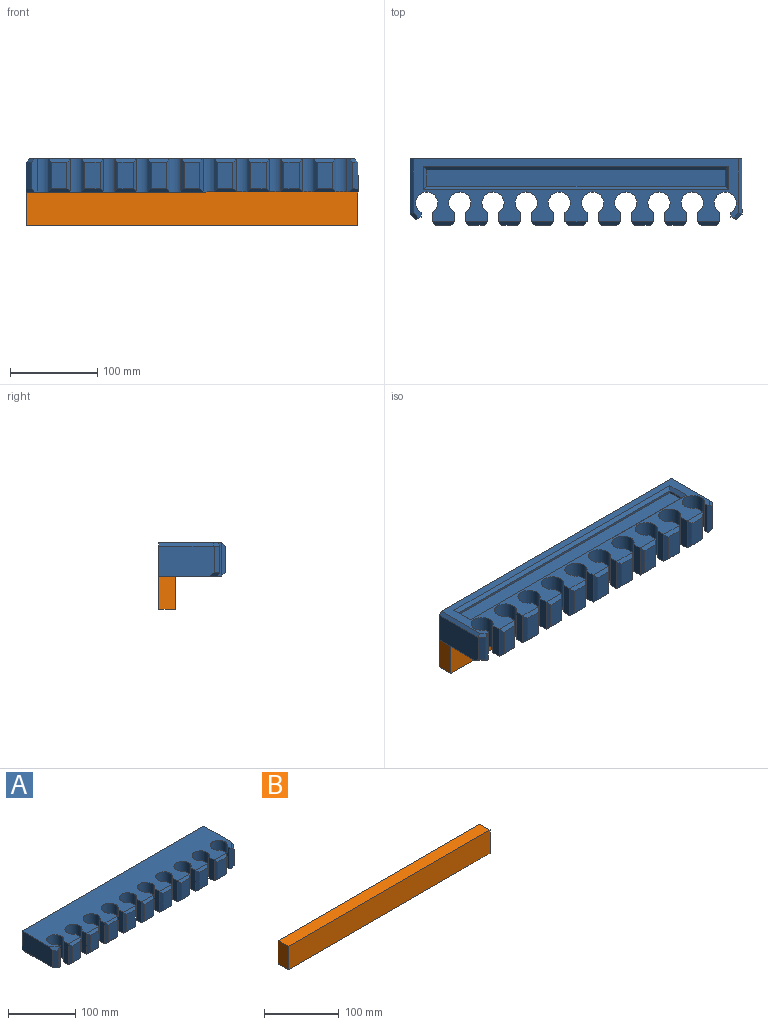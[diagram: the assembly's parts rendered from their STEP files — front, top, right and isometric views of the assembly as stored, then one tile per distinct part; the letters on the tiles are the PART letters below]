
ASSEMBLY  parts=2 mates=1
PART A: 99 faces, bbox 381x76.2x38.1 mm
  f0: plane 38.1x10.59mm, normal (-1,0,0), area 403.5mm2, adj f47,f48,f49,f86
  f1: plane 30.48x17.78mm, normal (0,-1,0), area 541.9mm2, adj f83,f84,f85,f86
  f2: plane 38.1x10.59mm, normal (1,0,0), area 403.5mm2, adj f3,f48,f49,f83
  f3: cylinder r=12.7mm len=38.1mm, axis (0,0,1), area 2533.5mm2, adj f2,f4,f48,f49
  f4: plane 38.1x10.59mm, normal (-1,0,0), area 403.5mm2, adj f3,f48,f49,f82
  f5: plane 30.48x17.78mm, normal (0,-1,0), area 541.9mm2, adj f79,f80,f81,f82
  f6: plane 38.1x10.59mm, normal (1,0,0), area 403.5mm2, adj f7,f48,f49,f79
  f7: cylinder r=12.7mm len=38.1mm, axis (0,0,1), area 2533.5mm2, adj f6,f8,f48,f49
  f8: plane 38.1x10.59mm, normal (-1,0,0), area 403.5mm2, adj f7,f48,f49,f78
  f9: plane 30.48x17.78mm, normal (0,-1,0), area 541.9mm2, adj f75,f76,f77,f78
  f10: plane 38.1x10.59mm, normal (1,0,0), area 403.5mm2, adj f11,f48,f49,f75
  f11: cylinder r=12.7mm len=38.1mm, axis (0,0,1), area 2533.5mm2, adj f10,f12,f48,f49
  f12: plane 38.1x10.59mm, normal (-1,0,0), area 403.5mm2, adj f11,f48,f49,f74
  f13: plane 30.48x17.78mm, normal (0,-1,0), area 541.9mm2, adj f71,f72,f73,f74
  f14: plane 38.1x10.59mm, normal (1,0,0), area 403.5mm2, adj f15,f48,f49,f71
  f15: cylinder r=12.7mm len=38.1mm, axis (0,0,1), area 2533.5mm2, adj f14,f16,f48,f49
  f16: plane 38.1x10.59mm, normal (-1,0,0), area 403.5mm2, adj f15,f48,f49,f70
  f17: plane 30.48x17.78mm, normal (0,-1,0), area 541.9mm2, adj f67,f68,f69,f70
  f18: plane 38.1x10.59mm, normal (1,0,0), area 403.5mm2, adj f19,f48,f49,f67
  f19: cylinder r=12.7mm len=38.1mm, axis (0,0,1), area 2533.5mm2, adj f18,f20,f48,f49
  f20: plane 38.1x10.59mm, normal (-1,0,0), area 403.5mm2, adj f19,f48,f49,f66
  f21: plane 30.48x17.78mm, normal (0,-1,0), area 541.9mm2, adj f63,f64,f65,f66
  f22: plane 38.1x10.59mm, normal (1,0,0), area 403.5mm2, adj f23,f48,f49,f63
  f23: cylinder r=12.7mm len=38.1mm, axis (0,0,1), area 2533.5mm2, adj f22,f24,f48,f49
  f24: plane 38.1x10.59mm, normal (-1,0,0), area 403.5mm2, adj f23,f48,f49,f62
  f25: plane 30.48x17.78mm, normal (0,-1,0), area 541.9mm2, adj f59,f60,f61,f62
  f26: plane 38.1x10.59mm, normal (1,0,0), area 403.5mm2, adj f27,f48,f49,f59
  f27: cylinder r=12.7mm len=38.1mm, axis (0,0,1), area 2533.5mm2, adj f26,f28,f48,f49
  f28: plane 38.1x10.59mm, normal (-1,0,0), area 403.5mm2, adj f27,f48,f49,f91
  f29: plane 30.48x17.78mm, normal (0,-1,0), area 541.9mm2, adj f91,f92,f93,f94
  f30: plane 38.1x10.59mm, normal (1,0,0), area 403.5mm2, adj f31,f48,f49,f94
  f31: cylinder r=12.7mm len=38.1mm, axis (0,0,1), area 2533.5mm2, adj f30,f32,f48,f49
  f32: plane 38.1x10.59mm, normal (-1,0,0), area 403.5mm2, adj f31,f48,f49,f58
  f33: plane 30.48x17.78mm, normal (0,-1,0), area 541.9mm2, adj f55,f56,f57,f58
  f34: plane 38.1x10.59mm, normal (1,0,0), area 403.5mm2, adj f35,f48,f49,f55
  f35: cylinder r=12.7mm len=38.1mm, axis (0,0,1), area 2533.5mm2, adj f34,f36,f48,f49
  f36: plane 38.1x5.2mm, normal (-1,0,0), area 198.2mm2, adj f35,f48,f49,f98
  f37: plane 30.48x6.2mm, normal (0.71,-0.71,0), area 267.1mm2, adj f38,f96,f97,f98
  f38: plane 63.5x34.29mm, normal (1,0,0), area 2167mm2, adj f37,f39,f49,f95,f97
  f39: plane 381x38.1mm, normal (0,1,0), area 14501.6mm2, adj f38,f40,f48,f49,f87,f95
  f40: plane 63.5x34.29mm, normal (-1,0,0), area 2167mm2, adj f39,f41,f49,f87,f89
  f41: plane 30.48x6.2mm, normal (-0.71,-0.71,0), area 267.1mm2, adj f40,f88,f89,f90
  f42: plane 38.1x5.2mm, normal (1,0,0), area 198.2mm2, adj f47,f48,f49,f90
  f43: plane 19.05x2.54mm, normal (-1,0,0), area 48.4mm2, adj f44,f46,f50,f54
  f44: plane 342.9x2.54mm, normal (0,1,0), area 871mm2, adj f43,f45,f50,f52
  f45: plane 19.05x2.54mm, normal (1,0,0), area 48.4mm2, adj f44,f46,f50,f51
  f46: plane 342.9x2.54mm, normal (0,-1,0), area 871mm2, adj f43,f45,f50,f53
  f47: cylinder r=12.7mm len=38.1mm, axis (0,0,1), area 2533.5mm2, adj f0,f42,f48,f49
  f48: plane 373.38x72.39mm, normal (0,0,-1), area 11297.1mm2, adj f0,f2,f3,f4,f6,f7,f8,f10
  f49: plane 381x72.39mm, normal (0,0,1), area 21102.8mm2, adj f0,f2,f3,f4,f6,f7,f8,f10
  f50: plane 342.9x19.05mm, normal (0,0,-1), area 6532.2mm2, adj f43,f44,f45,f46
  f51: plane 26.67x3.81mm, normal (0.71,0,-0.71), area 123.2mm2, adj f45,f48,f52,f53
  f52: plane 350.52x3.81mm, normal (0,0.71,-0.71), area 1868.1mm2, adj f44,f48,f51,f54
  f53: plane 350.52x3.81mm, normal (0,-0.71,-0.71), area 1868.1mm2, adj f46,f48,f51,f54
  f54: plane 26.67x3.81mm, normal (-0.71,0,-0.71), area 123.2mm2, adj f43,f48,f52,f53
  f55: plane 38.1x3.81mm, normal (0.71,-0.71,0), area 184.8mm2, adj f33,f34,f56,f57
  f56: plane 25.4x3.81mm, normal (0,-0.71,-0.71), area 116.3mm2, adj f33,f48,f55,f58
  f57: plane 25.4x3.81mm, normal (0,-0.71,0.71), area 116.3mm2, adj f33,f49,f55,f58
  f58: plane 38.1x3.81mm, normal (-0.71,-0.71,0), area 184.8mm2, adj f32,f33,f56,f57
  f59: plane 38.1x3.81mm, normal (0.71,-0.71,0), area 184.8mm2, adj f25,f26,f60,f61
  f60: plane 25.4x3.81mm, normal (0,-0.71,-0.71), area 116.3mm2, adj f25,f48,f59,f62
  f61: plane 25.4x3.81mm, normal (0,-0.71,0.71), area 116.3mm2, adj f25,f49,f59,f62
  f62: plane 38.1x3.81mm, normal (-0.71,-0.71,0), area 184.8mm2, adj f24,f25,f60,f61
  f63: plane 38.1x3.81mm, normal (0.71,-0.71,0), area 184.8mm2, adj f21,f22,f64,f65
  f64: plane 25.4x3.81mm, normal (0,-0.71,-0.71), area 116.3mm2, adj f21,f48,f63,f66
  f65: plane 25.4x3.81mm, normal (0,-0.71,0.71), area 116.3mm2, adj f21,f49,f63,f66
  f66: plane 38.1x3.81mm, normal (-0.71,-0.71,0), area 184.8mm2, adj f20,f21,f64,f65
  f67: plane 38.1x3.81mm, normal (0.71,-0.71,0), area 184.8mm2, adj f17,f18,f68,f69
  f68: plane 25.4x3.81mm, normal (0,-0.71,-0.71), area 116.3mm2, adj f17,f48,f67,f70
  f69: plane 25.4x3.81mm, normal (0,-0.71,0.71), area 116.3mm2, adj f17,f49,f67,f70
  f70: plane 38.1x3.81mm, normal (-0.71,-0.71,0), area 184.8mm2, adj f16,f17,f68,f69
  f71: plane 38.1x3.81mm, normal (0.71,-0.71,0), area 184.8mm2, adj f13,f14,f72,f73
  f72: plane 25.4x3.81mm, normal (0,-0.71,-0.71), area 116.3mm2, adj f13,f48,f71,f74
  f73: plane 25.4x3.81mm, normal (0,-0.71,0.71), area 116.3mm2, adj f13,f49,f71,f74
  f74: plane 38.1x3.81mm, normal (-0.71,-0.71,0), area 184.8mm2, adj f12,f13,f72,f73
  f75: plane 38.1x3.81mm, normal (0.71,-0.71,0), area 184.8mm2, adj f9,f10,f76,f77
  f76: plane 25.4x3.81mm, normal (0,-0.71,-0.71), area 116.3mm2, adj f9,f48,f75,f78
  f77: plane 25.4x3.81mm, normal (0,-0.71,0.71), area 116.3mm2, adj f9,f49,f75,f78
  f78: plane 38.1x3.81mm, normal (-0.71,-0.71,0), area 184.8mm2, adj f8,f9,f76,f77
  f79: plane 38.1x3.81mm, normal (0.71,-0.71,0), area 184.8mm2, adj f5,f6,f80,f81
  f80: plane 25.4x3.81mm, normal (0,-0.71,-0.71), area 116.3mm2, adj f5,f48,f79,f82
  f81: plane 25.4x3.81mm, normal (0,-0.71,0.71), area 116.3mm2, adj f5,f49,f79,f82
  f82: plane 38.1x3.81mm, normal (-0.71,-0.71,0), area 184.8mm2, adj f4,f5,f80,f81
  f83: plane 38.1x3.81mm, normal (0.71,-0.71,0), area 184.8mm2, adj f1,f2,f84,f85
  f84: plane 25.4x3.81mm, normal (0,-0.71,-0.71), area 116.3mm2, adj f1,f48,f83,f86
  f85: plane 25.4x3.81mm, normal (0,-0.71,0.71), area 116.3mm2, adj f1,f49,f83,f86
  f86: plane 38.1x3.81mm, normal (-0.71,-0.71,0), area 184.8mm2, adj f0,f1,f84,f85
  f87: plane 63.5x3.81mm, normal (-0.71,0,-0.71), area 337.9mm2, adj f39,f40,f48,f88
  f88: plane 10.01x7.78mm, normal (-0.5,-0.5,-0.71), area 47.2mm2, adj f41,f48,f87,f90
  f89: plane 11.59x10.01mm, normal (-0.5,-0.5,0.71), area 61.7mm2, adj f40,f41,f49,f90
  f90: plane 38.1x6.5mm, normal (0.38,-0.92,0), area 252.5mm2, adj f41,f42,f48,f49,f88,f89
  f91: plane 38.1x3.81mm, normal (-0.71,-0.71,0), area 184.8mm2, adj f28,f29,f92,f93
  f92: plane 25.4x3.81mm, normal (0,-0.71,-0.71), area 116.3mm2, adj f29,f48,f91,f94
  f93: plane 25.4x3.81mm, normal (0,-0.71,0.71), area 116.3mm2, adj f29,f49,f91,f94
  f94: plane 38.1x3.81mm, normal (0.71,-0.71,0), area 184.8mm2, adj f29,f30,f92,f93
  f95: plane 63.5x3.81mm, normal (0.71,0,-0.71), area 337.9mm2, adj f38,f39,f48,f96
  f96: plane 10.01x7.78mm, normal (0.5,-0.5,-0.71), area 47.2mm2, adj f37,f48,f95,f98
  f97: plane 11.59x10.01mm, normal (0.5,-0.5,0.71), area 61.7mm2, adj f37,f38,f49,f98
  f98: plane 38.1x6.5mm, normal (-0.38,-0.92,0), area 252.5mm2, adj f36,f37,f48,f49,f96,f97
PART B: 6 faces, bbox 381x19.1x38.1 mm
  f0: plane 381x38.1mm, normal (0,1,0), area 14516.1mm2, adj f1,f3,f4,f5
  f1: plane 381x19.05mm, normal (0,0,1), area 7258mm2, adj f0,f2,f4,f5
  f2: plane 381x38.1mm, normal (0,-1,0), area 14516.1mm2, adj f1,f3,f4,f5
  f3: plane 381x19.05mm, normal (0,0,-1), area 7258.1mm2, adj f0,f2,f4,f5
  f4: plane 38.1x19.05mm, normal (-1,0,0), area 725.8mm2, adj f0,f1,f2,f3
  f5: plane 38.1x19.05mm, normal (1,0,0), area 725.8mm2, adj f0,f1,f2,f3
PLACE A rot(axis=(0,1,0),180deg) t=(3.22,5.62,-30.54)mm
PLACE B rot(axis=(0,1,0),180deg) t=(-187.28,5.62,-68.64)mm
MATE parallel A.f49 <-> B.f3  axis (0,0,-1) through (-187.28,5.62,-30.54)mm
